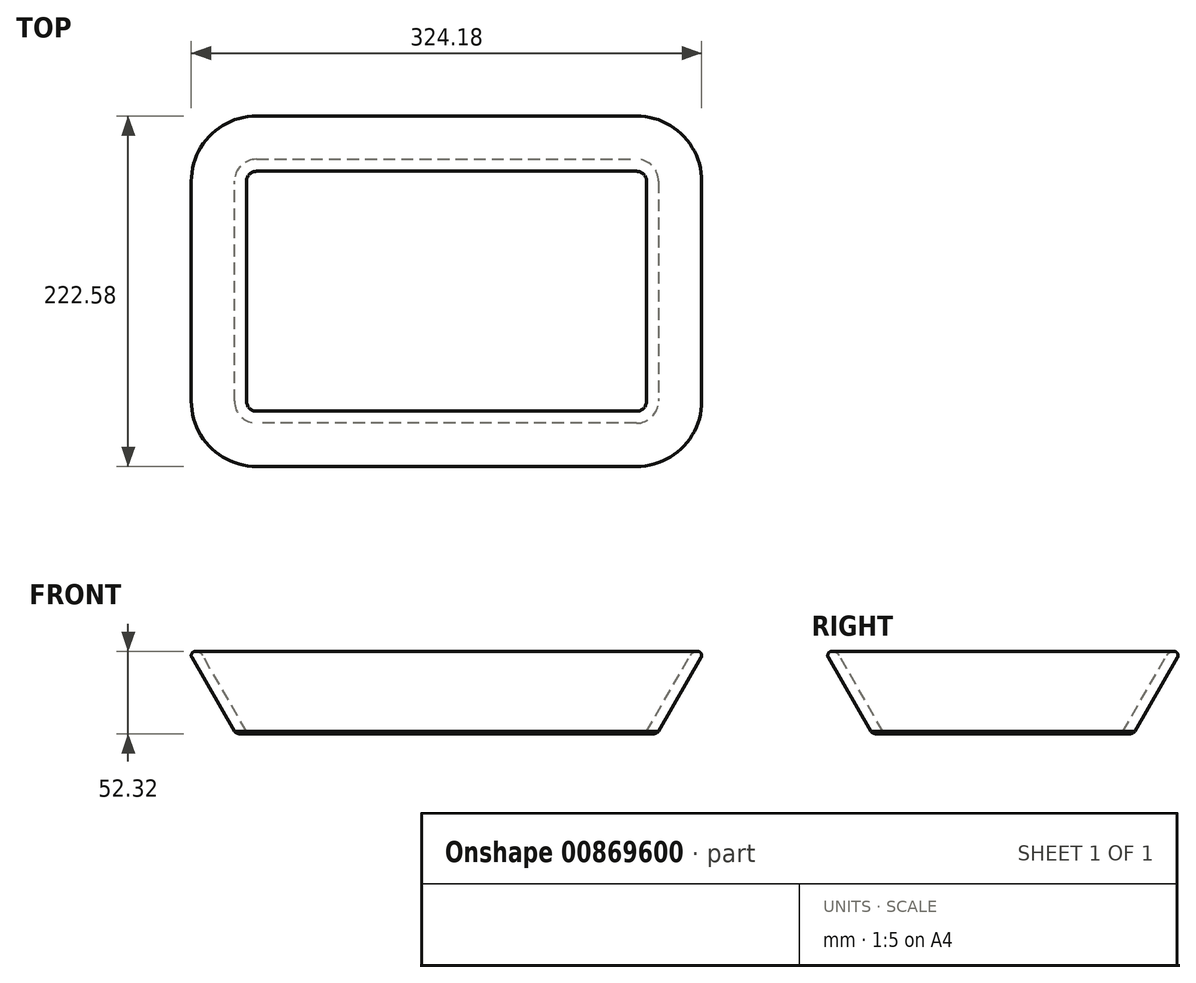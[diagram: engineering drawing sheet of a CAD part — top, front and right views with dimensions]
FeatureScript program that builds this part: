
annotation { "Feature Type Name" : "Feature", "Feature Type Description" : "" }
export const myFeature = defineFeature(function(context is Context, id is Id, definition is map)
    precondition{}
    {
        {
            var Q0;
            Q0=qCreatedBy(makeId("Top.planeOp"),FACE);
            var sketch = newSketch(context, id + "F0", { "sketchPlane" : qUnion([Q0])});
            skLineSegment(sketch, "E0.bottom", {"start": v(-310.41, 124.95) * mm, "end": v(-69.11, 124.95) * mm});
            skLineSegment(sketch, "E0.top", {"start": v(-310.41, -27.45) * mm, "end": v(-69.11, -27.45) * mm});
            skLineSegment(sketch, "E0.left", {"start": v(-316.76, 118.6) * mm, "end": v(-316.76, -21.1) * mm});
            skLineSegment(sketch, "E0.right", {"start": v(-62.76, 118.6) * mm, "end": v(-62.76, -21.1) * mm});
            skPoint(sketch, "E1.visualSharp", {"position": v(-316.76, 124.95) * mm});
            skArc(sketch, "E1.filletArc", {"start": v(-310.41, 124.95) * mm, "mid": v(-314.9, 123.1) * mm, "end": v(-316.76, 118.6) * mm});
            skPoint(sketch, "E2.visualSharp", {"position": v(-62.76, 124.95) * mm});
            skArc(sketch, "E2.filletArc", {"start": v(-62.76, 118.6) * mm, "mid": v(-64.62, 123.1) * mm, "end": v(-69.11, 124.95) * mm});
            skPoint(sketch, "E3.visualSharp", {"position": v(-62.76, -27.45) * mm});
            skArc(sketch, "E3.filletArc", {"start": v(-69.11, -27.45) * mm, "mid": v(-64.62, -25.59) * mm, "end": v(-62.76, -21.1) * mm});
            skPoint(sketch, "E4.visualSharp", {"position": v(-316.76, -27.45) * mm});
            skArc(sketch, "E4.filletArc", {"start": v(-316.76, -21.1) * mm, "mid": v(-314.9, -25.59) * mm, "end": v(-310.41, -27.45) * mm});
            skSolve(sketch);
        }
        {
            var Q0;
            Q0=qCreatedBy(makeId("Front.planeOp"),FACE);
            var sketch = newSketch(context, id + "F1", { "sketchPlane" : qUnion([Q0])});
            skPoint(sketch, "E5.0", {"position": v(-62.76, 0) * mm});
            skLineSegment(sketch, "E6", {"start": v(-62.76, 0) * mm, "end": v(-33.43, 50.8) * mm});
            skLineSegment(sketch, "E7", {"start": v(-33.43, 50.8) * mm, "end": v(-25.81, 50.8) * mm});
            skLineSegment(sketch, "E8", {"start": v(-25.81, 50.8) * mm, "end": v(-55.14, 0) * mm});
            skLineSegment(sketch, "E9", {"start": v(-55.14, 0) * mm, "end": v(-62.76, 0) * mm});
            skSolve(sketch);
        }
        {
            var Q0;
            Q0=makeQuery(id+"F1.imprint","IMPRINT",FACE,{"disambiguationData":[TD([[makeQuery(id+"F1.imprint","IMPRINT",EDGE,{"derivedFrom":sQuery(id+"F1.wireOp",EDGE,"E6")}),-1.0]])]});
            var Q1;
            Q1=sQuery(id+"F0.wireOp",EDGE,"E0.right");
            var Q2;
            Q2=sQuery(id+"F0.wireOp",EDGE,"E2.filletArc");
            var Q3;
            Q3=sQuery(id+"F0.wireOp",EDGE,"E0.bottom");
            var Q4;
            Q4=sQuery(id+"F0.wireOp",EDGE,"E1.filletArc");
            var Q5;
            Q5=sQuery(id+"F0.wireOp",EDGE,"E0.left");
            var Q6;
            Q6=sQuery(id+"F0.wireOp",EDGE,"E4.filletArc");
            var Q7;
            Q7=sQuery(id+"F0.wireOp",EDGE,"E0.top");
            var Q8;
            Q8=sQuery(id+"F0.wireOp",EDGE,"E3.filletArc");
            sweep(context, id + "F2", {"profiles" : qUnion([Q0]), "path" : qUnion([Q1, Q2, Q3, Q4, Q5, Q6, Q7, Q8])});
        }
        {
            var Q0;
            Q0=makeQuery(id+"F0.imprint","IMPRINT",FACE,{"disambiguationData":[TD([[makeQuery(id+"F0.imprint","IMPRINT",EDGE,{"derivedFrom":sQuery(id+"F0.wireOp",EDGE,"E0.bottom")}),-1.0]])]});
            extrude(context, id + "F3", {"entities" : qUnion([Q0]), "oppositeDirection" : true, "depth" : 1.52 * mm, "offsetDistance" : 25.4 * mm});
        }
        {
            var Q0;
            Q0=makeQuery(id+"F2.opSweep","SWEPT_FACE",FACE,{"disambiguationData":[OSD([sQuery(id+"F0.wireOp",EDGE,"E0.right"),sQuery(id+"F1.wireOp",EDGE,"E9")])]});
            var Q1;
            Q1=makeQuery(id+"F3.opExtrude","CAP_FACE",FACE,{"disambiguationData":[OSD([sQuery(id+"F0.wireOp",EDGE,"E0.bottom"),sQuery(id+"F0.wireOp",EDGE,"E0.top"),sQuery(id+"F0.wireOp",EDGE,"E0.left"),sQuery(id+"F0.wireOp",EDGE,"E0.right"),sQuery(id+"F0.wireOp",EDGE,"E1.filletArc"),sQuery(id+"F0.wireOp",EDGE,"E2.filletArc"),sQuery(id+"F0.wireOp",EDGE,"E3.filletArc"),sQuery(id+"F0.wireOp",EDGE,"E4.filletArc")])],"isStart":false});
            extrude(context, id + "F4", {"entities" : qUnion([Q0]), "operationType" : NewBodyOperationType.ADD, "endBound" : BoundingType.UP_TO_SURFACE, "depth" : 25.4 * mm, "endBoundEntityFace" : qUnion([Q1]), "offsetDistance" : 25.4 * mm});
        }
        {
            var Q0;
            Q0=makeQuery(id+"F4.opExtrude","CAP_EDGE",EDGE,{"disambiguationData":[OSD([sQuery(id+"F0.wireOp",EDGE,"E0.right"),sQuery(id+"F1.wireOp",EDGE,"E8"),sQuery(id+"F1.wireOp",EDGE,"E9")])],"isStart":false});
            fillet(context, id + "F5", {"entities" : qUnion([Q0]), "radius" : 5.08 * mm, "tangentPropagation" : true, "allowEdgeOverflow" : false});
        }
        {
            var Q0;
            Q0=makeQuery(id+"F2.opSweep","SWEPT_EDGE",EDGE,{"disambiguationData":[OSD([sQuery(id+"F0.wireOp",EDGE,"E0.right"),sQuery(id+"F1.wireOp",EDGE,"E7"),sQuery(id+"F1.wireOp",EDGE,"E8")])]});
            var Q1;
            Q1=makeQuery(id+"F2.opSweep","SWEPT_EDGE",EDGE,{"disambiguationData":[OSD([sQuery(id+"F0.wireOp",EDGE,"E3.filletArc"),sQuery(id+"F1.wireOp",EDGE,"E7"),sQuery(id+"F1.wireOp",EDGE,"E8")])]});
            var Q2;
            Q2=makeQuery(id+"F2.opSweep","SWEPT_EDGE",EDGE,{"disambiguationData":[OSD([sQuery(id+"F0.wireOp",EDGE,"E0.top"),sQuery(id+"F1.wireOp",EDGE,"E7"),sQuery(id+"F1.wireOp",EDGE,"E8")])]});
            var Q3;
            Q3=makeQuery(id+"F2.opSweep","SWEPT_EDGE",EDGE,{"disambiguationData":[OSD([sQuery(id+"F0.wireOp",EDGE,"E4.filletArc"),sQuery(id+"F1.wireOp",EDGE,"E7"),sQuery(id+"F1.wireOp",EDGE,"E8")])]});
            var Q4;
            Q4=makeQuery(id+"F2.opSweep","SWEPT_EDGE",EDGE,{"disambiguationData":[OSD([sQuery(id+"F0.wireOp",EDGE,"E0.left"),sQuery(id+"F1.wireOp",EDGE,"E7"),sQuery(id+"F1.wireOp",EDGE,"E8")])]});
            var Q5;
            Q5=makeQuery(id+"F2.opSweep","SWEPT_EDGE",EDGE,{"disambiguationData":[OSD([sQuery(id+"F0.wireOp",EDGE,"E1.filletArc"),sQuery(id+"F1.wireOp",EDGE,"E7"),sQuery(id+"F1.wireOp",EDGE,"E8")])]});
            var Q6;
            Q6=makeQuery(id+"F2.opSweep","SWEPT_EDGE",EDGE,{"disambiguationData":[OSD([sQuery(id+"F0.wireOp",EDGE,"E2.filletArc"),sQuery(id+"F1.wireOp",EDGE,"E7"),sQuery(id+"F1.wireOp",EDGE,"E8")])]});
            fillet(context, id + "F6", {"entities" : qUnion([Q0, Q1, Q2, Q3, Q4, Q5, Q6]), "radius" : 2.54 * mm, "tangentPropagation" : true, "allowEdgeOverflow" : false});
        }
        {
            var Q0;
            {var subQ0=sQuery(id+"F1.wireOp",EDGE,"E7");Q0=makeQuery(id+"F6.opFillet","BLEND_EDGE",EDGE,{"blendedFrom":[makeQuery(id+"F2.opSweep","SWEPT_EDGE",EDGE,{"disambiguationData":[OSD([sQuery(id+"F0.wireOp",EDGE,"E0.bottom"),subQ0,sQuery(id+"F1.wireOp",EDGE,"E8")])]}),makeQuery(id+"F2.opSweep","SWEPT_FACE",FACE,{"disambiguationData":[OSD([sQuery(id+"F0.wireOp",EDGE,"E0.right"),subQ0])]})],"blendedInto":[makeQuery(id+"F2.opSweep","SWEPT_FACE",FACE,{"disambiguationData":[OSD([sQuery(id+"F0.wireOp",EDGE,"E0.right"),subQ0])]})]});}
            var Q1;
            Q1=makeQuery(id+"F2.opSweep","SWEPT_EDGE",EDGE,{"disambiguationData":[OSD([sQuery(id+"F0.wireOp",EDGE,"E0.right"),sQuery(id+"F1.wireOp",EDGE,"E6"),sQuery(id+"F1.wireOp",EDGE,"E7")])]});
            var Q2;
            Q2=makeQuery(id+"F2.opSweep","SWEPT_EDGE",EDGE,{"disambiguationData":[OSD([sQuery(id+"F0.wireOp",EDGE,"E2.filletArc"),sQuery(id+"F1.wireOp",EDGE,"E6"),sQuery(id+"F1.wireOp",EDGE,"E7")])]});
            var Q3;
            Q3=makeQuery(id+"F2.opSweep","SWEPT_EDGE",EDGE,{"disambiguationData":[OSD([sQuery(id+"F0.wireOp",EDGE,"E0.bottom"),sQuery(id+"F1.wireOp",EDGE,"E6"),sQuery(id+"F1.wireOp",EDGE,"E7")])]});
            var Q4;
            Q4=makeQuery(id+"F2.opSweep","SWEPT_EDGE",EDGE,{"disambiguationData":[OSD([sQuery(id+"F0.wireOp",EDGE,"E3.filletArc"),sQuery(id+"F1.wireOp",EDGE,"E6"),sQuery(id+"F1.wireOp",EDGE,"E7")])]});
            var Q5;
            Q5=makeQuery(id+"F2.opSweep","SWEPT_EDGE",EDGE,{"disambiguationData":[OSD([sQuery(id+"F0.wireOp",EDGE,"E0.top"),sQuery(id+"F1.wireOp",EDGE,"E6"),sQuery(id+"F1.wireOp",EDGE,"E7")])]});
            var Q6;
            Q6=makeQuery(id+"F2.opSweep","SWEPT_EDGE",EDGE,{"disambiguationData":[OSD([sQuery(id+"F0.wireOp",EDGE,"E4.filletArc"),sQuery(id+"F1.wireOp",EDGE,"E6"),sQuery(id+"F1.wireOp",EDGE,"E7")])]});
            var Q7;
            Q7=makeQuery(id+"F2.opSweep","SWEPT_EDGE",EDGE,{"disambiguationData":[OSD([sQuery(id+"F0.wireOp",EDGE,"E0.left"),sQuery(id+"F1.wireOp",EDGE,"E6"),sQuery(id+"F1.wireOp",EDGE,"E7")])]});
            var Q8;
            Q8=makeQuery(id+"F2.opSweep","SWEPT_EDGE",EDGE,{"disambiguationData":[OSD([sQuery(id+"F0.wireOp",EDGE,"E1.filletArc"),sQuery(id+"F1.wireOp",EDGE,"E6"),sQuery(id+"F1.wireOp",EDGE,"E7")])]});
            fillet(context, id + "F7", {"entities" : qUnion([Q0, Q1, Q2, Q3, Q4, Q5, Q6, Q7, Q8]), "radius" : 5.08 * mm, "tangentPropagation" : true, "allowEdgeOverflow" : false});
        }
    });
